# Revit family: hansgrohe_56044XXX-RainDrain-Flex-Linear-shower-dr
name_source: partatom
category: Generic Models
revit_build: Autodesk Revit 2018 (Build: 20170223_1515(x64)
units: mm (PartAtom-declared; Revit-internal decimal feet)

## family parameters
Always vertical = No
Can host rebar = No
Cut with Voids When Loaded = No
Part Type = Normal
Room Calculation Point = No
Round Connector Dimension = Use Diameter
Shared = No
Work Plane-Based = No

## types (1)
- Default
    Brand url = http://www.hansgrohe-int.com
    Design country = Germany
    Edition number = 1
    GTIN code = https://4059625350119
    IFC Classification = Sanitary Terminal
    Installation instructions = https://www.hansgrohe.com
    Manufacturer country = Germany
    Manufacturer name = hansgrohe
    Material = Hansgrohe - Paket Wright - 140 Brushed Bronze
    Material main = Stainless steel
    Product Guid = ab232447-e1ee-47ce-b681-1d46e33511b8
    Product SKU = 56044XXX
    Product data url = https://bimobject.com
    Product family = RainDrain Flex
    Product group = Shower drains
    Product name = 56044XXX RainDrain Flex Linear shower drain 80 cm cuttable for free mounting
    Product url = https://www.hansgrohe.com
    QR code = http://bimobject.com
    Technical description = https://www.hansgrohe.com

## geometry (parser evidence)
native form markers: Sweep x2
no freeform markers — native parametric forms only
